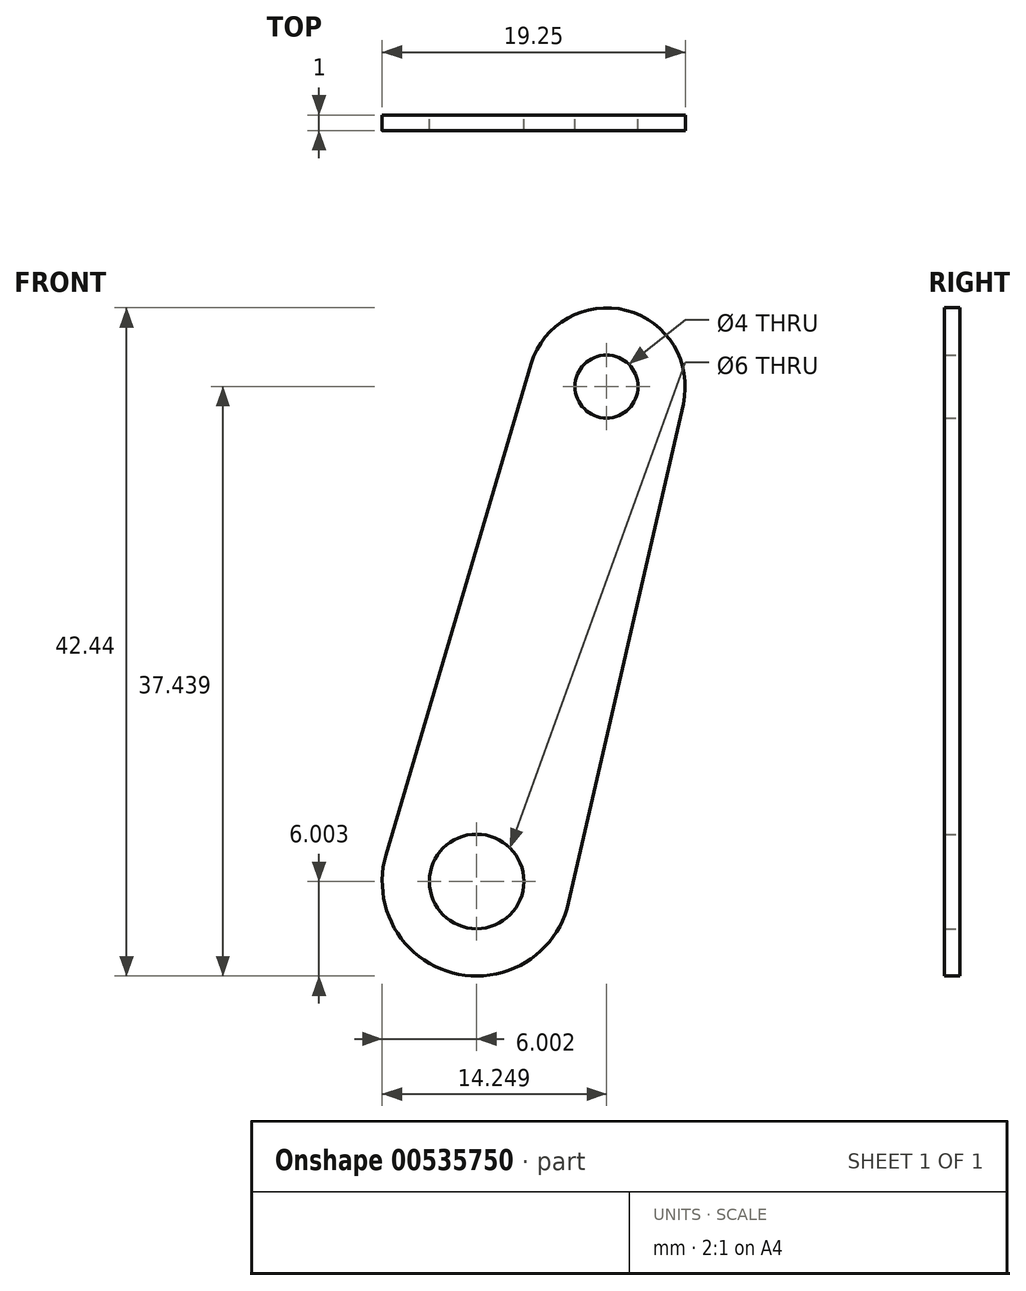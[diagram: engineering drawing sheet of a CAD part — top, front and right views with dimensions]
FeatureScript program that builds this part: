
annotation { "Feature Type Name" : "Feature", "Feature Type Description" : "" }
export const myFeature = defineFeature(function(context is Context, id is Id, definition is map)
    precondition{}
    {
        {
            var Q0;
            Q0=qCreatedBy(makeId("Front.planeOp"),FACE);
            var sketch = newSketch(context, id + "F0", { "sketchPlane" : qUnion([Q0])});
            skCircle(sketch, "E0", {"center": v(-22.16, 9.2) * mm, "radius": 2 * mm});
            skArc(sketch, "E1", {"start": v(-17.29, 8.08) * mm, "mid": v(-20.9, 14.04) * mm, "end": v(-26.96, 10.62) * mm});
            skArc(sketch, "E2", {"start": v(-36.16, -20.54) * mm, "mid": v(-31.93, -28.04) * mm, "end": v(-24.56, -23.58) * mm});
            skCircle(sketch, "E3", {"center": v(-30.4, -22.24) * mm, "radius": 3 * mm});
            skLineSegment(sketch, "E4", {"start": v(-36.16, -20.54) * mm, "end": v(-26.96, 10.62) * mm});
            skLineSegment(sketch, "E5", {"start": v(-17.29, 8.08) * mm, "end": v(-24.56, -23.58) * mm});
            skSolve(sketch);
        }
        {
            var Q0;
            Q0 = qSketchRegion(id + "F0", true);
            extrude(context, id + "F1", {"entities" : qUnion([Q0]), "endBound" : BoundingType.SYMMETRIC, "depth" : 1 * mm, "offsetDistance" : 25 * mm});
        }
    });
